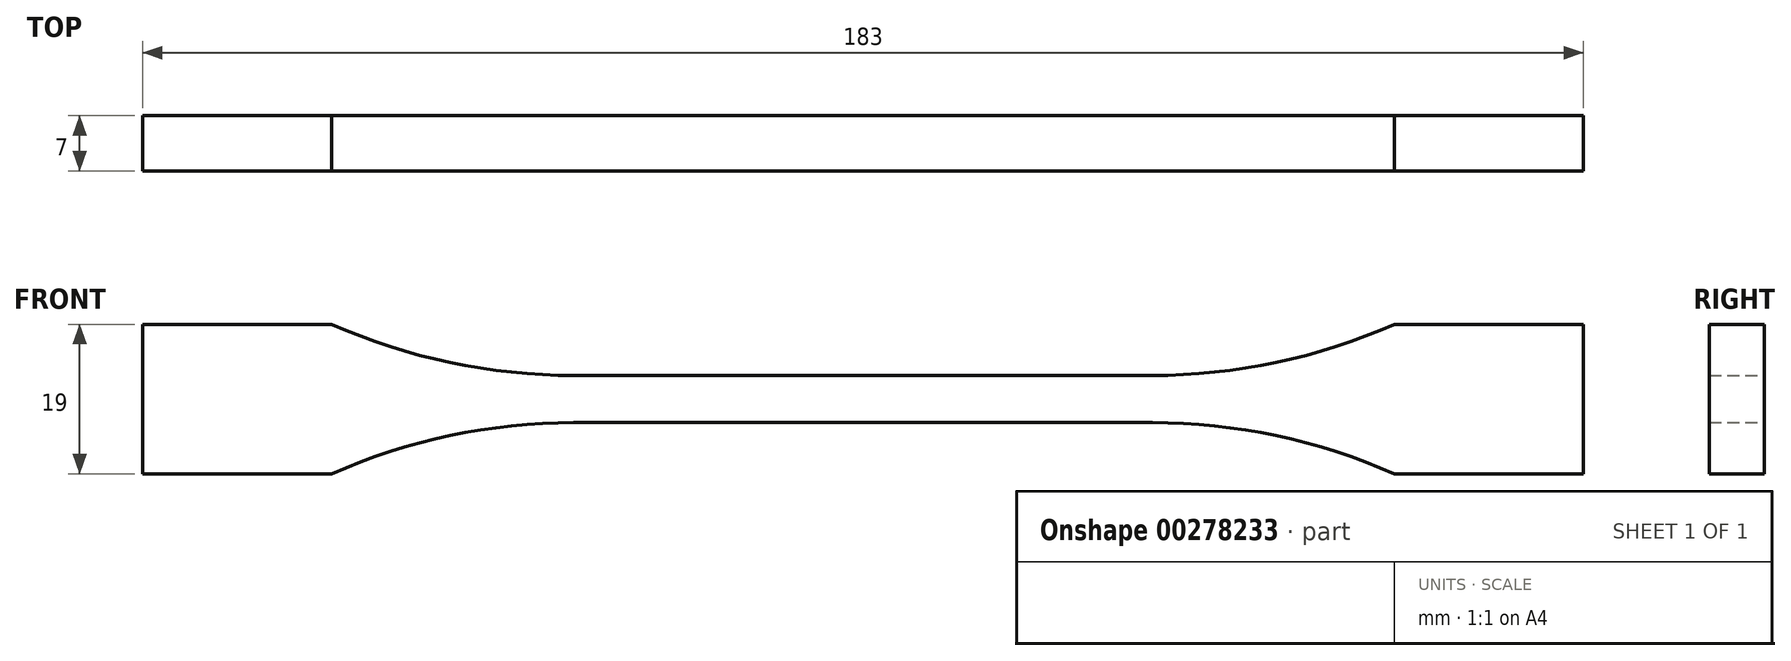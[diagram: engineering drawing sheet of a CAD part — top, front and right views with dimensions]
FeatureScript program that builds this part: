
annotation { "Feature Type Name" : "Feature", "Feature Type Description" : "" }
export const myFeature = defineFeature(function(context is Context, id is Id, definition is map)
    precondition{}
    {
        {
            var Q0;
            Q0=qCreatedBy(makeId("Front.planeOp"),FACE);
            var sketch = newSketch(context, id + "F0", { "sketchPlane" : qUnion([Q0])});
            skLineSegment(sketch, "E0", {"start": v(0, 3) * mm, "end": v(36.75, 3) * mm});
            skArc(sketch, "E1", {"start": v(36.75, 3) * mm, "mid": v(52.46, 4.64) * mm, "end": v(67.5, 9.5) * mm});
            skLineSegment(sketch, "E2", {"start": v(67.5, 9.5) * mm, "end": v(91.5, 9.5) * mm});
            skLineSegment(sketch, "E3.MirrorCS", {"start": v(67.5, -9.5) * mm, "end": v(91.5, -9.5) * mm});
            skLineSegment(sketch, "E4.MirrorCS", {"start": v(0, -3) * mm, "end": v(36.75, -3) * mm});
            skArc(sketch, "E5.MirrorCS", {"start": v(36.75, -3) * mm, "mid": v(52.46, -4.64) * mm, "end": v(67.5, -9.5) * mm});
            skArc(sketch, "E6.MirrorCS", {"start": v(-36.75, -3) * mm, "mid": v(-52.46, -4.64) * mm, "end": v(-67.5, -9.5) * mm});
            skLineSegment(sketch, "E7.MirrorCS", {"start": v(0, 3) * mm, "end": v(-36.75, 3) * mm});
            skArc(sketch, "E8.MirrorCS", {"start": v(-36.75, 3) * mm, "mid": v(-52.46, 4.64) * mm, "end": v(-67.5, 9.5) * mm});
            skLineSegment(sketch, "E9.MirrorCS", {"start": v(-67.5, -9.5) * mm, "end": v(-91.5, -9.5) * mm});
            skLineSegment(sketch, "E10.MirrorCS", {"start": v(0, -3) * mm, "end": v(-36.75, -3) * mm});
            skLineSegment(sketch, "E11.MirrorCS", {"start": v(-67.5, 9.5) * mm, "end": v(-91.5, 9.5) * mm});
            skLineSegment(sketch, "E12", {"start": v(-91.5, 9.5) * mm, "end": v(-91.5, -9.5) * mm});
            skLineSegment(sketch, "E13", {"start": v(91.5, 9.5) * mm, "end": v(91.5, -9.5) * mm});
            skSolve(sketch);
        }
        {
            var Q0;
            Q0 = qSketchRegion(id + "F0", true);
            extrude(context, id + "F1", {"entities" : qUnion([Q0]), "endBound" : BoundingType.SYMMETRIC, "depth" : 7 * mm});
        }
    });
